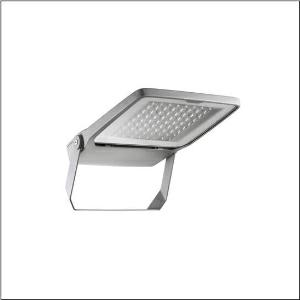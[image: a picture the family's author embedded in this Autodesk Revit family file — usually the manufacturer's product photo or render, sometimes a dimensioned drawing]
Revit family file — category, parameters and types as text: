
# Revit family: floodlight_fl_20_mini___pl43_5xa7671b2a1kc_a64d
name_source: partatom
category: Lighting Fixtures
units: mm (PartAtom-declared; Revit-internal decimal feet)

## family parameters
Cut with Voids When Loaded = No
Host = Face
Light Source = No
Part Type = Normal
Room Calculation Point = No
Round Connector Dimension = Use Diameter
Shared = No

## types (1)
- Floodlight FL 20 mini  PL43 (1 x LED 4000K / CRI = 70 (unbekannt), 6650 lm, 4000K)
    Apparent Load = 51 VA
    CIE Flux Codes = 32 74 99 100 100
    Color Rendering = 70
    Color Temperature = 4000K
    Default Elevation = 1800 mm
    Description = Floodlight FL 20 mini, floodlight, primary light control with lens, of plastic, primary optical cover: protective disc, of toughened safety glass, transparent, light distribution: PL43, light emission: direct distribution, primary light characteristic: asymmetric, installation type: surface-mounted, LED, High Power LED, rated luminous flux: 6.650lm, luminous efficacy: 130lm/W, light colour: 740, colour temperature: 4000K, control gear: ECG Basic, control: power reduction, overheat protection, electronic power reduction, with terminal, 5-pole, max. 2.5mm², mains connection: 220..240V, AC, 50/60Hz, rated input power: 51W, LED unit, of diecast aluminium, powder-coated, Siteco® metallic grey (DB 702S), corrosivity category C5 mid according to DIN EN ISO 12944, incl. 1x M20 cable gland for cable Ø 6.5..12mm, length: 446mm, width: 355mm, height: 62mm, housing frame, of diecast aluminium, powder-coated, Siteco® metallic grey (DB 702S), mounting bracket, of steel, powder-coated, Siteco® metallic grey (DB 702S), ON/OFF, protection rating (complete): IP66, insulation class (complete): insulation class I (protective earthing), certification: CE, ENEC, VDE, protection symbol: D, permissible operating ambient temperature: -40..+40°C, permissible operating ambient temperature for outdoor applications: -40..+50°C, standard: DIN EN 12944, packaging unit: 1 piece

Light Distribution: PL43
    Height = 62 mm  [stored 0.203412 ft]
    Lamp = 1 x LED 4000K / CRI >= 70 (unbekannt)
    Lamp Light Flux = 6650 lm
    Lamp count = 1
    Length = 467 mm
    Luminous efficacy = 130 lm/W
    Manufacturer = Siteco
    ModVariant = No
    Model = 5XA7671B2A1KC
    Mounting Place = Wall
    Mounting Type = Surface mounted
    Number of Poles = 1
    OnlyDefault = Yes
    Power Factor = 1
    Product Name = Floodlight FL 20 mini | PL43
    Product group = floodlight | wall mounted
    ProductGroupID = 2001
    Protection Class = Protection class I
    Protection Degree = IP 66
    RLX_Detail_Level = 1
    RLX_Emergency_Light_Flux = 0 lm
    RLX_Emergency_Type = 0
    RLX_Emergency_Type_DB = No
    RlxData = <blob elided: 70869 chars, md5=718b6ed1>
    Socket = socket
    Standby Power = 0 W
    System Light Flux = 6650 lm
    System Power = 51 W
    Type Comments = Product without accessories
    Type Image = l_1005948.jpg
    URL = http://relux.com
    VarID = ---
    Voltage = 0 V
    Weight = 0.00 kg
    Width = 335 mm

note: [stored X ft] marks values corroborated as IEEE doubles in the binary element streams (Revit-internal decimal feet)

## geometry (parser evidence)
native form markers: Blend x4, Sweep x12
no freeform markers — native parametric forms only
